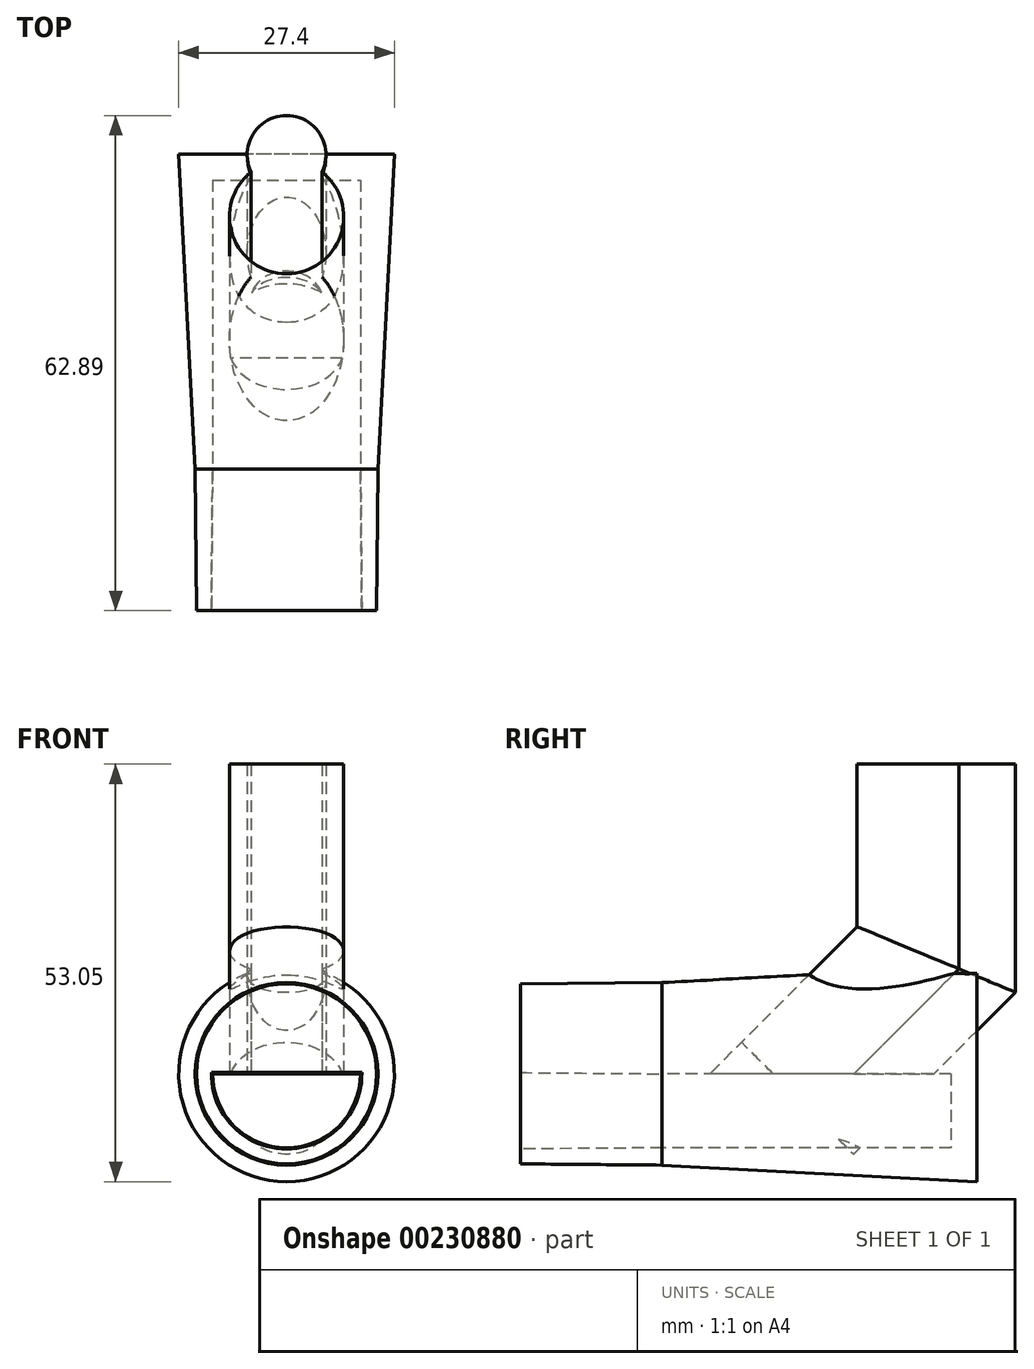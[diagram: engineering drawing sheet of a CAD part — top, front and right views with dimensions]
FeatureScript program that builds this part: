
annotation { "Feature Type Name" : "Feature", "Feature Type Description" : "" }
export const myFeature = defineFeature(function(context is Context, id is Id, definition is map)
    precondition{}
    {
        {
            var Q0;
            Q0=qCreatedBy(makeId("Front.planeOp"),FACE);
            var sketch = newSketch(context, id + "F0", { "sketchPlane" : qUnion([Q0])});
            skCircle(sketch, "E0", {"center": v(0, 0) * mm, "radius": 11.6 * mm});
            skCircle(sketch, "E1.0", {"center": v(0, 0) * mm, "radius": 9.4 * mm, "construction": true});
            skLineSegment(sketch, "E2", {"start": v(-9.4, 0) * mm, "end": v(9.4, 0) * mm});
            skArc(sketch, "E3", {"start": v(-9.4, 0) * mm, "mid": v(0, -9.4) * mm, "end": v(9.4, 0) * mm});
            skSolve(sketch);
        }
        {
            var Q0;
            Q0 = qSketchRegion(id + "F0", true);
            extrude(context, id + "F1", {"entities" : qUnion([Q0]), "depth" : 18 * mm, "hasDraft" : true, "draftAngle" : .5 * degree, "draftPullDirection" : true});
        }
        {
            var Q0;
            Q0=qCreatedBy(makeId("Right.planeOp"),FACE);
            var sketch = newSketch(context, id + "F2", { "sketchPlane" : qUnion([Q0])});
            skLineSegment(sketch, "E4", {"start": v(18, -3.9) * mm, "end": v(35.96, 14.06) * mm});
            skLineSegment(sketch, "E5", {"start": v(35.96, 14.06) * mm, "end": v(35.96, 39.35) * mm});
            skSolve(sketch);
        }
        {
            var Q0;
            Q0=qCreatedBy(makeId("Top.planeOp"),FACE);
            var Q1;
            Q1=sQuery(id+"F2.wireOp",VERTEX,"E5.end");
            cPlane(context, id + "F3", {"entities" : qUnion([Q0, Q1]), "cplaneType" : CPlaneType.PLANE_POINT, "offset" : 25 * mm, "width" : 150 * mm, "height" : 150 * mm});
        }
        {
            var Q0;
            Q0=qCreatedBy(id+"F3.planeOp",FACE);
            var sketch = newSketch(context, id + "F4", { "sketchPlane" : qUnion([Q0])});
            skCircle(sketch, "E6", {"center": v(0, 32.03) * mm, "radius": 7.25 * mm});
            skCircle(sketch, "E7", {"center": v(0, 39.9) * mm, "radius": 5 * mm});
            skLineSegment(sketch, "E8", {"start": v(-4.5, 37.71) * mm, "end": v(4.5, 37.71) * mm, "construction": true});
            skLineSegment(sketch, "E9", {"start": v(0, 32.03) * mm, "end": v(0, 39.9) * mm, "construction": true});
            skSolve(sketch);
        }
        {
            var Q0;
            Q0 = qSketchRegion(id + "F4", true);
            var Q1;
            Q1=sQuery(id+"F2.wireOp",EDGE,"E5");
            var Q2;
            Q2=sQuery(id+"F2.wireOp",EDGE,"E4");
            sweep(context, id + "F5", {"profiles" : qUnion([Q0]), "path" : qUnion([Q1, Q2])});
        }
        {
            var Q0;
            Q0=makeQuery(id+"F1.opExtrude","CAP_FACE",FACE,{"disambiguationData":[OSD([sQuery(id+"F0.wireOp",EDGE,"E0"),sQuery(id+"F0.wireOp",EDGE,"E2"),sQuery(id+"F0.wireOp",EDGE,"E3")])],"isStart":true});
            var sketch = newSketch(context, id + "F6", { "sketchPlane" : qUnion([Q0])});
            skCircle(sketch, "E10.0", {"center": v(0, 0) * mm, "radius": 11.6 * mm});
            skSolve(sketch);
        }
        {
            var Q0;
            Q0 = qSketchRegion(id + "F6", true);
            extrude(context, id + "F7", {"entities" : qUnion([Q0]), "depth" : 40 * mm, "hasDraft" : true, "draftAngle" : 3 * degree});
        }
        {
            var Q0;
            Q0=makeQuery(id+"F5.opSweep","SWEPT_BODY",BODY,{"disambiguationData":[OSD([sQuery(id+"F2.wireOp",EDGE,"E4"),sQuery(id+"F4.wireOp",EDGE,"E6"),sQuery(id+"F4.wireOp",EDGE,"E7")])]});
            var Q1;
            Q1=makeQuery(id+"F7.opExtrude","SWEPT_BODY",BODY,{"disambiguationData":[OSD([sQuery(id+"F6.wireOp",EDGE,"E10.0")])]});
            booleanBodies(context, id + "F8", {"operationType" : BooleanOperationType.SUBTRACTION, "tools" : qUnion([Q0]), "targets" : qUnion([Q1]), "keepTools" : true});
        }
        {
            var Q0;
            Q0=makeQuery(id+"F7.opExtrude","CAP_FACE",FACE,{"disambiguationData":[OSD([sQuery(id+"F6.wireOp",EDGE,"E10.0")])],"isStart":true});
            var sketch = newSketch(context, id + "F9", { "sketchPlane" : qUnion([Q0])});
            skArc(sketch, "E11.0", {"start": v(-9.4, 0) * mm, "mid": v(0, -9.4) * mm, "end": v(9.4, 0) * mm});
            skLineSegment(sketch, "E11.1", {"start": v(-9.4, 0) * mm, "end": v(9.4, 0) * mm});
            skSolve(sketch);
        }
        {
            var Q0;
            Q0 = qSketchRegion(id + "F9", true);
            extrude(context, id + "F10", {"entities" : qUnion([Q0]), "operationType" : NewBodyOperationType.REMOVE, "oppositeDirection" : true, "depth" : 36.7 * mm});
        }
        {
            var Q0;
            {var subQ0=sQuery(id+"F4.wireOp",EDGE,"E6");Q0=makeQuery(id+"F10.boolean.opBoolean","SPLIT",FACE,{"disambiguationData":[TD([makeQuery(id+"F10.opExtrude","SWEPT_FACE",FACE,{"disambiguationData":[OSD([sQuery(id+"F9.wireOp",EDGE,"E11.1")])]})])],"derivedFrom":makeQuery(id+"F8.opBoolean","COPY",FACE,{"derivedFrom":makeQuery(id+"F5.opSweep","CAP_FACE",FACE,{"disambiguationData":[OSD([sQuery(id+"F2.wireOp",VERTEX,"E4.start"),subQ0,sQuery(id+"F4.wireOp",EDGE,"E7")])],"isStart":false})})});}
            extrude(context, id + "F11", {"entities" : qUnion([Q0]), "operationType" : NewBodyOperationType.REMOVE, "endBound" : BoundingType.UP_TO_NEXT, "oppositeDirection" : true, "depth" : 25 * mm});
        }
    });
